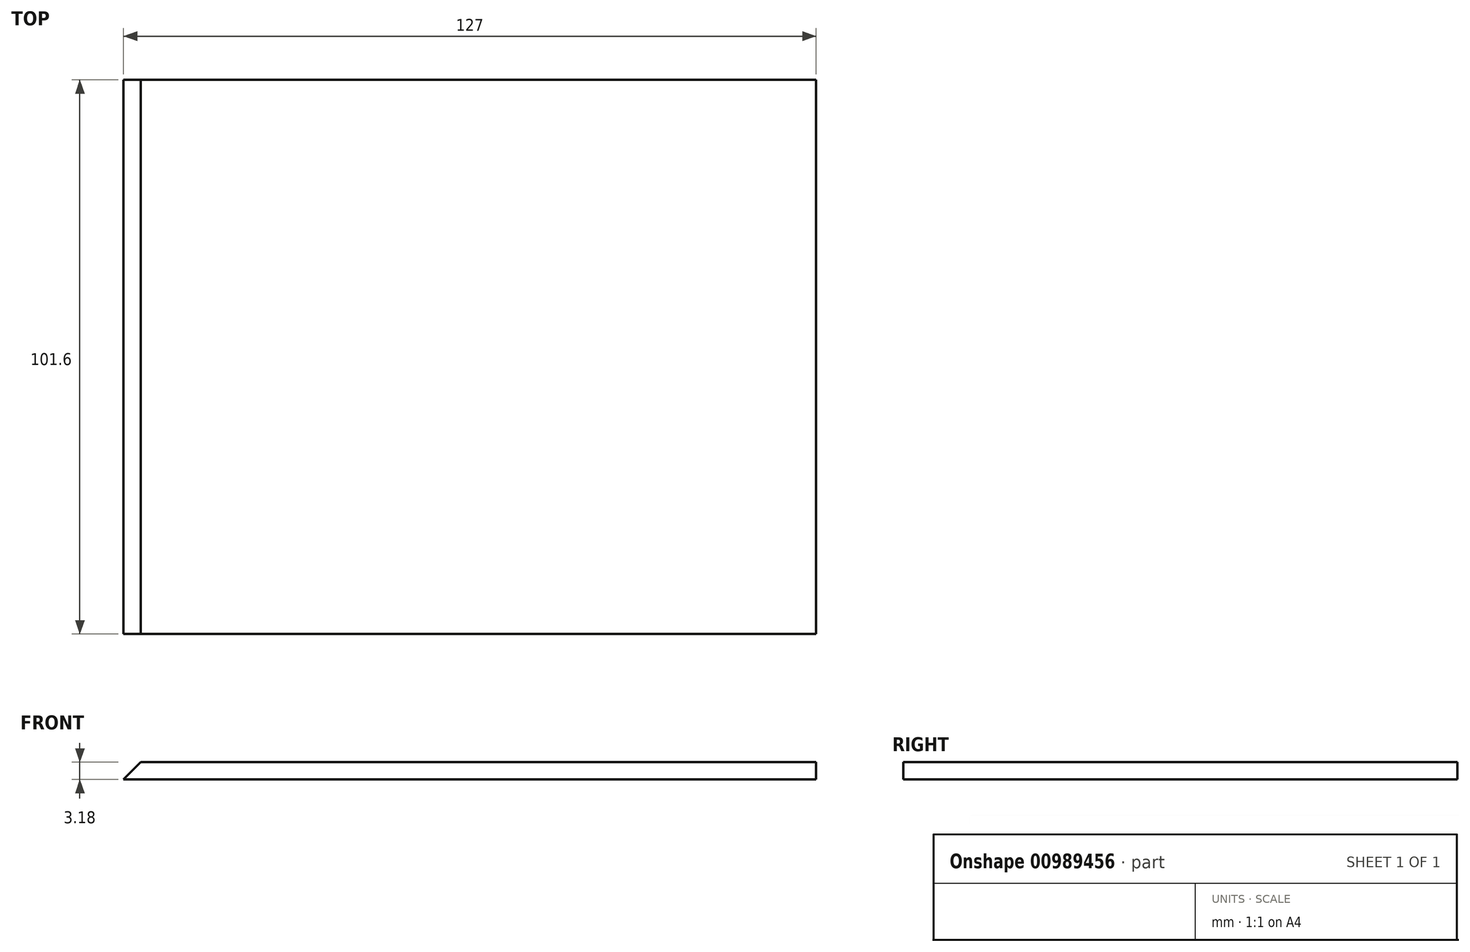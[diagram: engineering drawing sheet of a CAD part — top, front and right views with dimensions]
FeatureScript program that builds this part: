
annotation { "Feature Type Name" : "Feature", "Feature Type Description" : "" }
export const myFeature = defineFeature(function(context is Context, id is Id, definition is map)
    precondition{}
    {
        {
            var Q0;
            Q0=qCreatedBy(makeId("Front.planeOp"),FACE);
            var sketch = newSketch(context, id + "F0", { "sketchPlane" : qUnion([Q0])});
            skLineSegment(sketch, "E0.bottom", {"start": v(63.5, 1.59) * mm, "end": v(-60.32, 1.59) * mm});
            skLineSegment(sketch, "E0.top", {"start": v(63.5, -1.59) * mm, "end": v(-63.5, -1.59) * mm});
            skLineSegment(sketch, "E0.left", {"start": v(63.5, 1.59) * mm, "end": v(63.5, -1.59) * mm});
            skPoint(sketch, "E0.middle", {"position": v(0, 0) * mm});
            skLineSegment(sketch, "E1", {"start": v(-63.5, -1.59) * mm, "end": v(-60.32, 1.59) * mm});
            skPoint(sketch, "E2.orphan", {"position": v(-63.5, 1.59) * mm});
            skSolve(sketch);
        }
        {
            var Q0;
            Q0 = qSketchRegion(id + "F0", true);
            extrude(context, id + "F1", {"entities" : qUnion([Q0]), "endBound" : BoundingType.SYMMETRIC, "depth" : 101.6 * mm, "offsetDistance" : 25.4 * mm});
        }
    });
